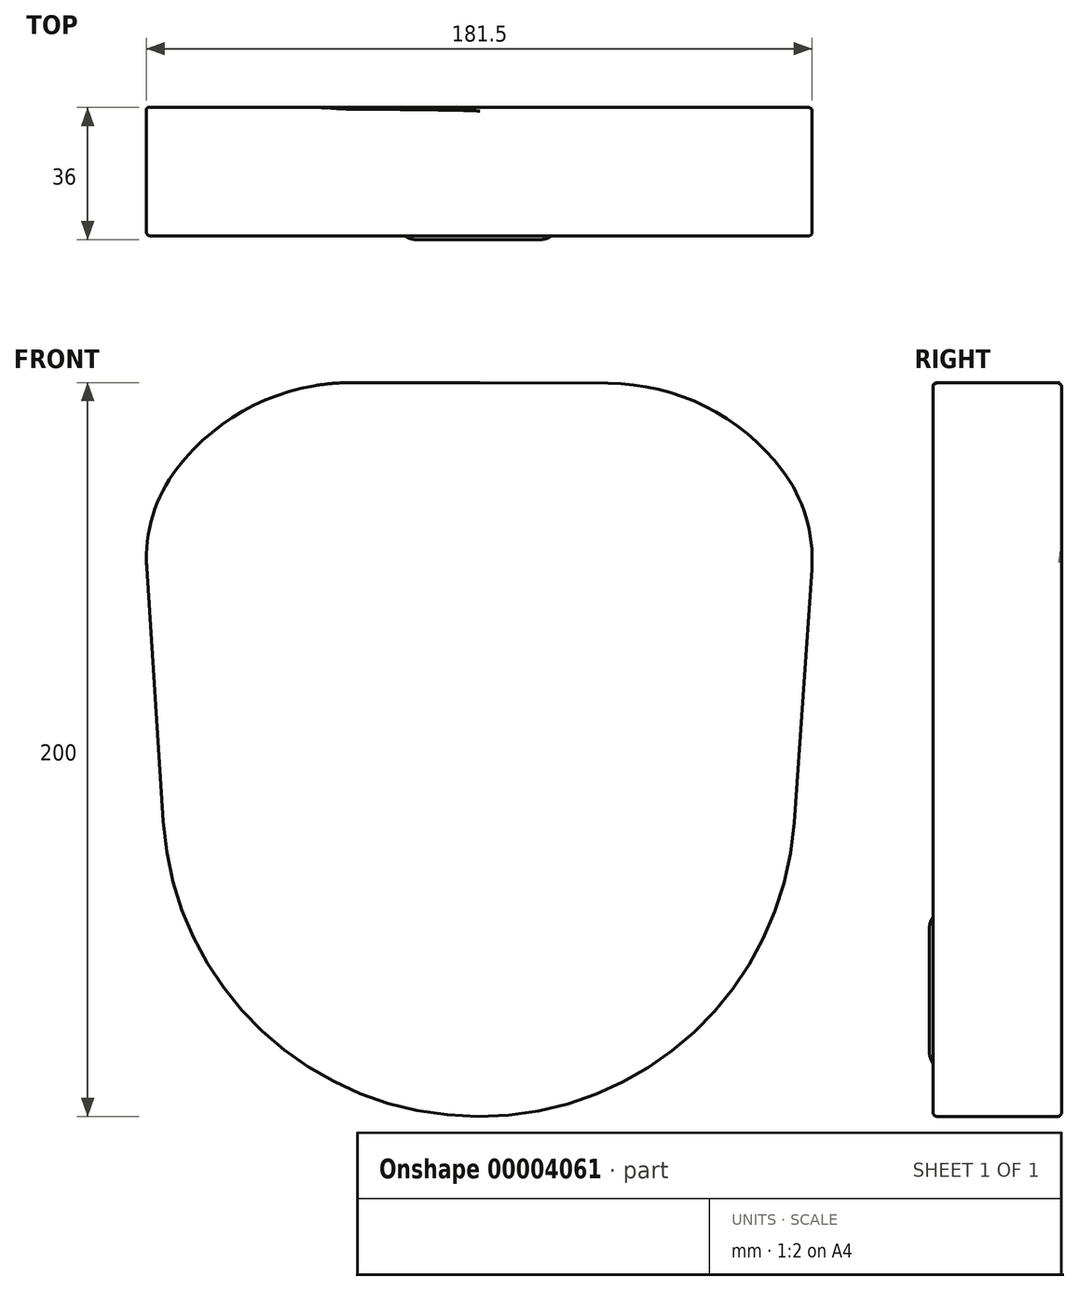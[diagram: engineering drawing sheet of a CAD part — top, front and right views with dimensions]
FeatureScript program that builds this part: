
annotation { "Feature Type Name" : "Feature", "Feature Type Description" : "" }
export const myFeature = defineFeature(function(context is Context, id is Id, definition is map)
    precondition{}
    {
        {
            var Q0;
            Q0=qCreatedBy(makeId("Front.planeOp"),FACE);
            var sketch = newSketch(context, id + "F0", { "sketchPlane" : qUnion([Q0])});
            skLineSegment(sketch, "E0.bottom", {"start": v(-34.52, 60) * mm, "end": v(0.48, 60) * mm});
            skLineSegment(sketch, "E0.top", {"start": v(0, -140) * mm, "end": v(0, -140) * mm});
            skLineSegment(sketch, "E0.right", {"start": v(0.48, 60) * mm, "end": v(0, -140) * mm});
            skPoint(sketch, "E1.visualSharp", {"position": v(-71.08, 60) * mm});
            skArc(sketch, "E1.filletArc", {"start": v(-34.52, 60) * mm, "mid": v(-69.05, 49.07) * mm, "end": v(-91, 20.27) * mm});
            skLineSegment(sketch, "E2", {"start": v(-91, 20.27) * mm, "end": v(-85.82, -59.56) * mm});
            skPoint(sketch, "E3.visualSharp", {"position": v(-80.6, -140) * mm});
            skArc(sketch, "E3.filletArc", {"start": v(-85.82, -59.56) * mm, "mid": v(-58.81, -116.75) * mm, "end": v(0, -140) * mm});
            skLineSegment(sketch, "E4.0.MirrorCS", {"start": v(35.48, 59.83) * mm, "end": v(0.48, 60) * mm});
            skArc(sketch, "E5.0.MirrorCS", {"start": v(35.48, 59.83) * mm, "mid": v(69.95, 48.74) * mm, "end": v(91.76, 19.83) * mm});
            skLineSegment(sketch, "E6.0.MirrorCS", {"start": v(91.76, 19.83) * mm, "end": v(86.2, -59.97) * mm});
            skArc(sketch, "E7.0.MirrorCS", {"start": v(86.2, -59.97) * mm, "mid": v(58.92, -117.03) * mm, "end": v(0, -140) * mm});
            skCircle(sketch, "E8", {"center": v(0.08, -105.6) * mm, "radius": 20 * mm});
            skSolve(sketch);
        }
        {
            var Q0;
            Q0 = qSketchRegion(id + "F0", true);
            var Q1;
            {var subQ0=sQuery(id+"F0.wireOp",EDGE,"E8");var subQ1=sQuery(id+"F0.wireOp",EDGE,"E0.right");var subQ3=makeQuery(id+"F0.imprint","INTERSECT",VERTEX,{"disambiguationData":[OD(0.0)],"derivedFrom":[subQ1,subQ0]});Q1=makeQuery(id+"F0.imprint","IMPRINT",FACE,{"disambiguationData":[TD([[makeQuery(id+"F0.imprint","IMPRINT",EDGE,{"disambiguationData":[TD([[subQ3,-1.0]])],"derivedFrom":subQ1}),-1.0]])]});}
            var Q2;
            {var subQ0=sQuery(id+"F0.wireOp",EDGE,"E8");var subQ1=sQuery(id+"F0.wireOp",EDGE,"E0.right");var subQ3=makeQuery(id+"F0.imprint","INTERSECT",VERTEX,{"disambiguationData":[OD(0.0)],"derivedFrom":[subQ1,subQ0]});Q2=makeQuery(id+"F0.imprint","IMPRINT",FACE,{"disambiguationData":[TD([[makeQuery(id+"F0.imprint","IMPRINT",EDGE,{"disambiguationData":[TD([[subQ3,-1.0]])],"derivedFrom":subQ1}),1.0]])]});}
            var Q3;
            {var subQ1=sQuery(id+"F0.wireOp",EDGE,"E0.right");var subQ4=sQuery(id+"F0.wireOp",EDGE,"b1be69c9-5e5d-459a-8c3c-74bf074e2bd7");var subQ6=makeQuery(id+"F0.imprint","INTERSECT",VERTEX,{"disambiguationData":[OD(0.0)],"derivedFrom":[subQ1,subQ4]});Q3=makeQuery(id+"F0.imprint","IMPRINT",FACE,{"disambiguationData":[TD([[makeQuery(id+"F0.imprint","IMPRINT",EDGE,{"disambiguationData":[TD([[subQ6,-1.0]])],"derivedFrom":subQ1}),1.0]])]});}
            var Q4;
            {var subQ1=sQuery(id+"F0.wireOp",EDGE,"E0.right");var subQ4=sQuery(id+"F0.wireOp",EDGE,"b1be69c9-5e5d-459a-8c3c-74bf074e2bd7");var subQ6=makeQuery(id+"F0.imprint","INTERSECT",VERTEX,{"disambiguationData":[OD(0.0)],"derivedFrom":[subQ1,subQ4]});Q4=makeQuery(id+"F0.imprint","IMPRINT",FACE,{"disambiguationData":[TD([[makeQuery(id+"F0.imprint","IMPRINT",EDGE,{"disambiguationData":[TD([[subQ6,-1.0]])],"derivedFrom":subQ1}),-1.0]])]});}
            extrude(context, id + "F1", {"entities" : qUnion([Q0, Q1, Q2, Q3, Q4]), "depth" : 10 * mm});
        }
        {
            var Q0;
            {var subQ0=sQuery(id+"F0.wireOp",EDGE,"E8");var subQ1=sQuery(id+"F0.wireOp",EDGE,"E0.right");var subQ3=makeQuery(id+"F0.imprint","INTERSECT",VERTEX,{"disambiguationData":[OD(0.0)],"derivedFrom":[subQ1,subQ0]});Q0=makeQuery(id+"F0.imprint","IMPRINT",FACE,{"disambiguationData":[TD([[makeQuery(id+"F0.imprint","IMPRINT",EDGE,{"disambiguationData":[TD([[subQ3,-1.0]])],"derivedFrom":subQ1}),-1.0]])]});}
            var Q1;
            {var subQ0=sQuery(id+"F0.wireOp",EDGE,"E8");var subQ1=sQuery(id+"F0.wireOp",EDGE,"E0.right");var subQ3=makeQuery(id+"F0.imprint","INTERSECT",VERTEX,{"disambiguationData":[OD(0.0)],"derivedFrom":[subQ1,subQ0]});Q1=makeQuery(id+"F0.imprint","IMPRINT",FACE,{"disambiguationData":[TD([[makeQuery(id+"F0.imprint","IMPRINT",EDGE,{"disambiguationData":[TD([[subQ3,-1.0]])],"derivedFrom":subQ1}),1.0]])]});}
            extrude(context, id + "F2", {"entities" : qUnion([Q0, Q1]), "operationType" : NewBodyOperationType.ADD, "depth" : 11 * mm});
        }
        {
            var Q0;
            Q0=makeQuery(id+"F2.opExtrude","CAP_FACE",FACE,{"disambiguationData":[OSD([sQuery(id+"F0.wireOp",EDGE,"E8")])],"isStart":false});
            fillet(context, id + "F3", {"entities" : qUnion([Q0]), "radius" : 5 * mm, "tangentPropagation" : true, "allowEdgeOverflow" : false});
        }
        {
            var Q0;
            {var subQ5=sQuery(id+"F0.wireOp",EDGE,"E0.bottom");Q0=makeQuery(id+"F0.imprint","IMPRINT",FACE,{"disambiguationData":[TD([[makeQuery(id+"F0.imprint","IMPRINT",EDGE,{"derivedFrom":subQ5}),-1.0]])]});}
            var Q1;
            {var subQ1=sQuery(id+"F0.wireOp",EDGE,"E4.0.MirrorCS");Q1=makeQuery(id+"F0.imprint","IMPRINT",FACE,{"disambiguationData":[TD([[makeQuery(id+"F0.imprint","IMPRINT",EDGE,{"derivedFrom":subQ1}),1.0]])]});}
            var Q2;
            {var subQ0=sQuery(id+"F0.wireOp",EDGE,"E8");var subQ1=sQuery(id+"F0.wireOp",EDGE,"E0.right");var subQ3=makeQuery(id+"F0.imprint","INTERSECT",VERTEX,{"disambiguationData":[OD(0.0)],"derivedFrom":[subQ1,subQ0]});Q2=makeQuery(id+"F0.imprint","IMPRINT",FACE,{"disambiguationData":[TD([[makeQuery(id+"F0.imprint","IMPRINT",EDGE,{"disambiguationData":[TD([[subQ3,-1.0]])],"derivedFrom":subQ1}),1.0]])]});}
            var Q3;
            {var subQ0=sQuery(id+"F0.wireOp",EDGE,"E8");var subQ1=sQuery(id+"F0.wireOp",EDGE,"E0.right");var subQ3=makeQuery(id+"F0.imprint","INTERSECT",VERTEX,{"disambiguationData":[OD(0.0)],"derivedFrom":[subQ1,subQ0]});Q3=makeQuery(id+"F0.imprint","IMPRINT",FACE,{"disambiguationData":[TD([[makeQuery(id+"F0.imprint","IMPRINT",EDGE,{"disambiguationData":[TD([[subQ3,-1.0]])],"derivedFrom":subQ1}),-1.0]])]});}
            extrude(context, id + "F4", {"entities" : qUnion([Q0, Q1, Q2, Q3]), "operationType" : NewBodyOperationType.ADD, "oppositeDirection" : true, "depth" : 25 * mm});
        }
        {
            var Q0;
            {var subQ0=sQuery(id+"F0.wireOp",EDGE,"E5.0.MirrorCS");var subQ1=sQuery(id+"F0.wireOp",EDGE,"E6.0.MirrorCS");Q0=makeQuery(id+"F4.boolean.opBoolean","MERGE",EDGE,{"derivedFrom":[makeQuery(id+"F1.opExtrude","SWEPT_EDGE",EDGE,{"disambiguationData":[OSD([subQ0,subQ1])]}),makeQuery(id+"F4.opExtrude","SWEPT_EDGE",EDGE,{"disambiguationData":[OSD([subQ0,subQ1])]})]});}
            fillet(context, id + "F5", {"entities" : qUnion([Q0]), "radius" : 40 * mm, "tangentPropagation" : true, "allowEdgeOverflow" : false});
        }
        {
            var Q0;
            {var subQ0=sQuery(id+"F0.wireOp",EDGE,"E1.filletArc");var subQ1=sQuery(id+"F0.wireOp",EDGE,"E2");Q0=makeQuery(id+"F4.boolean.opBoolean","MERGE",EDGE,{"derivedFrom":[makeQuery(id+"F1.opExtrude","SWEPT_EDGE",EDGE,{"disambiguationData":[OSD([subQ0,subQ1])]}),makeQuery(id+"F4.opExtrude","SWEPT_EDGE",EDGE,{"disambiguationData":[OSD([subQ0,subQ1])]})]});}
            fillet(context, id + "F6", {"entities" : qUnion([Q0]), "radius" : 40 * mm, "tangentPropagation" : true, "allowEdgeOverflow" : false});
        }
        {
            var Q0;
            Q0=makeQuery(id+"F1.opExtrude","CAP_FACE",FACE,{"disambiguationData":[OSD([sQuery(id+"F0.wireOp",EDGE,"E0.bottom"),sQuery(id+"F0.wireOp",EDGE,"E1.filletArc"),sQuery(id+"F0.wireOp",EDGE,"E2"),sQuery(id+"F0.wireOp",EDGE,"E3.filletArc"),sQuery(id+"F0.wireOp",EDGE,"E4.0.MirrorCS"),sQuery(id+"F0.wireOp",EDGE,"E5.0.MirrorCS"),sQuery(id+"F0.wireOp",EDGE,"E6.0.MirrorCS"),sQuery(id+"F0.wireOp",EDGE,"E7.0.MirrorCS")])],"isStart":false});
            var Q1;
            {var subQ0=sQuery(id+"F0.wireOp",EDGE,"E6.0.MirrorCS");Q1=makeQuery(id+"F4.boolean.opBoolean","MERGE",FACE,{"derivedFrom":[makeQuery(id+"F1.opExtrude","SWEPT_FACE",FACE,{"disambiguationData":[OSD([subQ0])]}),makeQuery(id+"F4.opExtrude","SWEPT_FACE",FACE,{"disambiguationData":[OSD([subQ0])]})]});}
            fillet(context, id + "F7", {"entities" : qUnion([Q0, Q1]), "radius" : 1 * mm, "tangentPropagation" : true, "allowEdgeOverflow" : false});
        }
    });
